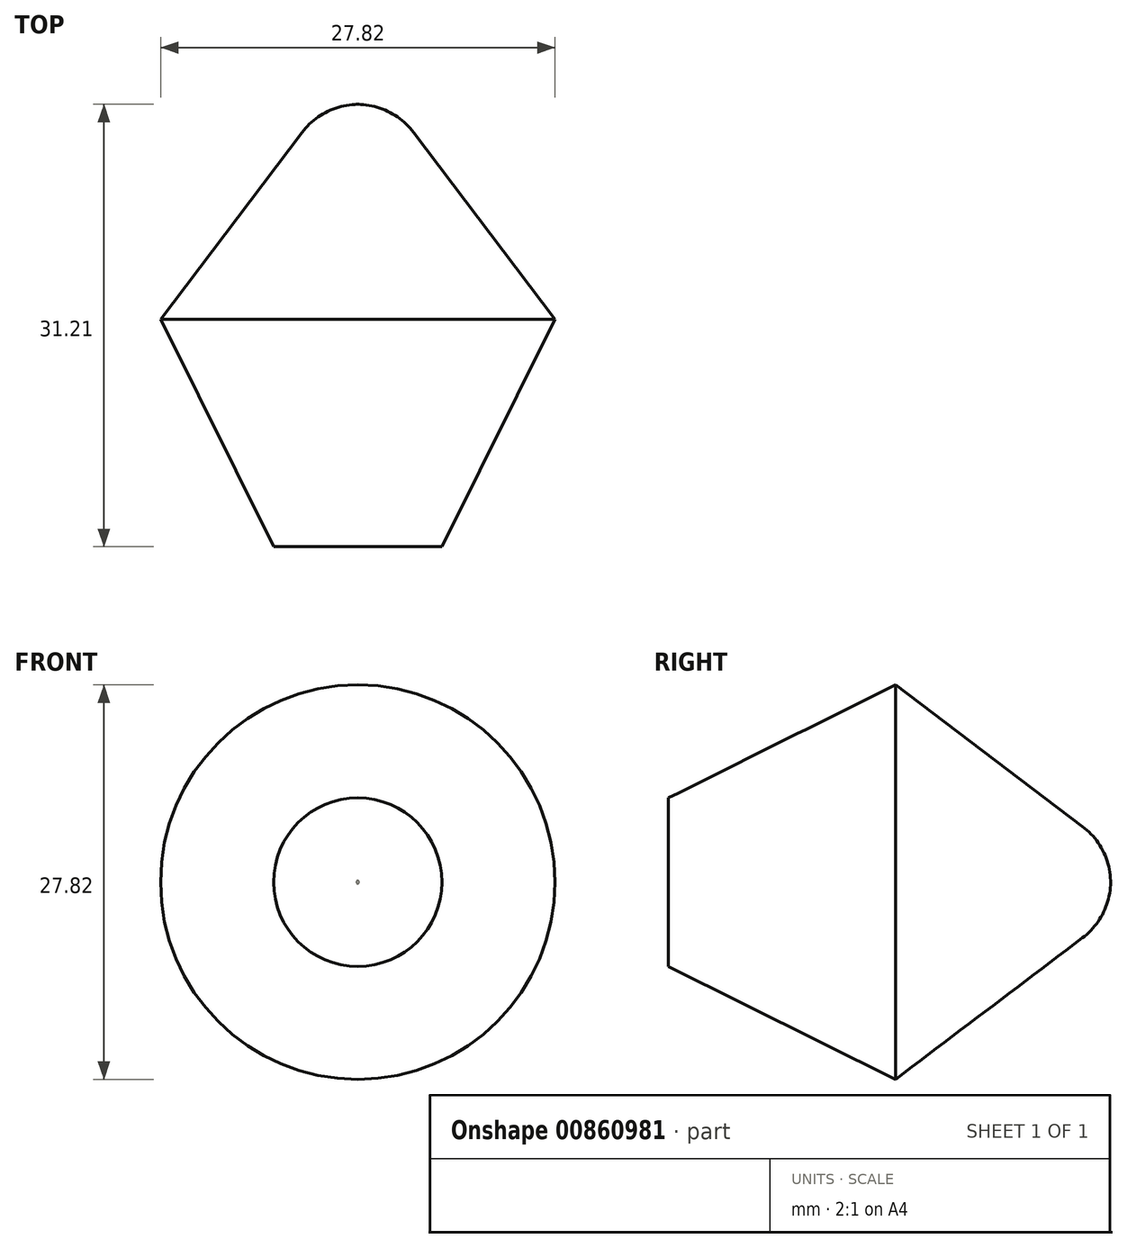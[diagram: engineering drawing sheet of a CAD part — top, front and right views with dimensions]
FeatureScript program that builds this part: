
annotation { "Feature Type Name" : "Feature", "Feature Type Description" : "" }
export const myFeature = defineFeature(function(context is Context, id is Id, definition is map)
    precondition{}
    {
        {
            var Q0;
            Q0=qCreatedBy(makeId("Top.planeOp"),FACE);
            var sketch = newSketch(context, id + "F0", { "sketchPlane" : qUnion([Q0])});
            skLineSegment(sketch, "E0", {"start": v(-26.74, 0) * mm, "end": v(-4, 29.28) * mm});
            skLineSegment(sketch, "E1", {"start": v(3.94, 29.23) * mm, "end": v(26.04, 0) * mm});
            skLineSegment(sketch, "E2", {"start": v(26.04, 0) * mm, "end": v(-26.74, 0) * mm});
            skPoint(sketch, "E3.visualSharp", {"position": v(0, 34.43) * mm});
            skArc(sketch, "E3.filletArc", {"start": v(3.94, 29.23) * mm, "mid": v(-0.02, 31.2) * mm, "end": v(-4, 29.28) * mm});
            skLineSegment(sketch, "E4", {"start": v(0, 0) * mm, "end": v(0, 31.2) * mm});
            skPoint(sketch, "E4.endSnap0", {"position": v(-0.02, 31.2) * mm});
            skSolve(sketch);
        }
        {
            var Q0;
            {var subQ0=sQuery(id+"F0.wireOp",EDGE,"E1");Q0=makeQuery(id+"F0.imprint","IMPRINT",FACE,{"disambiguationData":[TD([[makeQuery(id+"F0.imprint","IMPRINT",EDGE,{"derivedFrom":subQ0}),-1.0]])]});}
            var Q1;
            Q1=sQuery(id+"F0.wireOp",EDGE,"E4");
            revolve(context, id + "F1", {"surfaceOperationType" : NewSurfaceOperationType.NEW, "entities" : qUnion([Q0]), "axis" : qUnion([Q1]), "revolveType" : RevolveType.FULL});
        }
        {
            var Q0;
            Q0=makeQuery(id+"F1.opRevolve","SWEPT_EDGE",EDGE,{"disambiguationData":[OSD([sQuery(id+"F0.wireOp",EDGE,"E1"),sQuery(id+"F0.wireOp",EDGE,"E2")])]});
            chamfer(context, id + "F2", {"entities" : qUnion([Q0]), "width" : 10 * mm, "tangentPropagation" : true});
        }
    });
